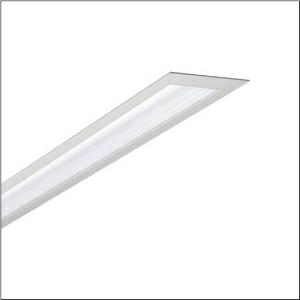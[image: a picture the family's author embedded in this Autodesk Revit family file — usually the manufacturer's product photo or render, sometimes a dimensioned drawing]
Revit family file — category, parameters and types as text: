
# Revit family: silica_r_5mx11bd1w4a_3352
name_source: partatom
category: Lighting Fixtures
units: mm (PartAtom-declared; Revit-internal decimal feet)

## family parameters
Cut with Voids When Loaded = No
Host = Face
Light Source = No
Part Type = Normal
Room Calculation Point = No
Round Connector Dimension = Use Diameter
Shared = No

## types (1)
- --- (1 x LED, 4950 lm, 29.3 W, 4000K)
    Apparent Load = 29 VA
    CIE Flux Codes = 82 97 100 100 100
    Color Rendering = 80
    Color Temperature = 4000K
    Default Elevation = 1800 mm
    Description = Silica®, office luminaire, of aluminium, light emission: direct distribution, primary light characteristic: symmetric, installation type: recessed, LED rated luminous flux: 4.950 lm, light colour: 840, colour temperature: 4000K, control gear: ECG DALI, with terminal, 3+2-pole, max. 2.5mm², mains connection: 230V, AC, 50/60Hz, rated input power: 29W, luminaire housing, of aluminium, matt pure white (RAL 9010), length: 1.462 mm, width: 93 mm, height: 60mm, end cap, of diecast zinc, pure white (RAL 9010), protection rating (complete): IP20, insulation class (complete): insulation class I (protective earthing), certification: CE, permissible ambient temperature for indoor applications: 0..+35°C, standard: EN 50419, packaging unit: 1 piece
    Height = 0 mm  [stored 0 ft]
    Lamp = 1 x LED
    Lamp Light Flux = 4950 lm
    Lamp Power = 29.3 W
    Lamp count = 1
    Length = 1462 mm
    Luminous efficacy = 169 lm/W
    Manufacturer = Siteco
    ModVariant = No
    Model = 5MX11BD1W4A
    Mounting Place = Ceiling
    Mounting Type = Recessed
    Number of Poles = 1
    OnlyDefault = Yes
    Power Factor = 1
    Product Name = Silica®
    Product group = office luminaire | ceiling recessed
    ProductGroupID = 400
    Protection Class = Protection class I
    Protection Degree = IP 20
    RLX_Detail_Level = 1
    RlxData = <blob elided: 24009 chars, md5=1f969f8d>
    Socket = socket
    Standby Power = 0 W
    System Light Flux = 4950 lm
    System Power = 29 W
    Type Comments = factory setting: luminous flux: 100 % | dim-lin: 254 | 163 mA
    Type Image = l_1004825.jpg
    URL = http://relux.com
    VarID = @adj_132064
    Voltage = 0 V
    Weight = 0.00 kg
    Width = 93 mm

note: [stored X ft] marks values corroborated as IEEE doubles in the binary element streams (Revit-internal decimal feet)

## geometry (parser evidence)
native form markers: Blend x4, Sweep x13
no freeform markers — native parametric forms only
